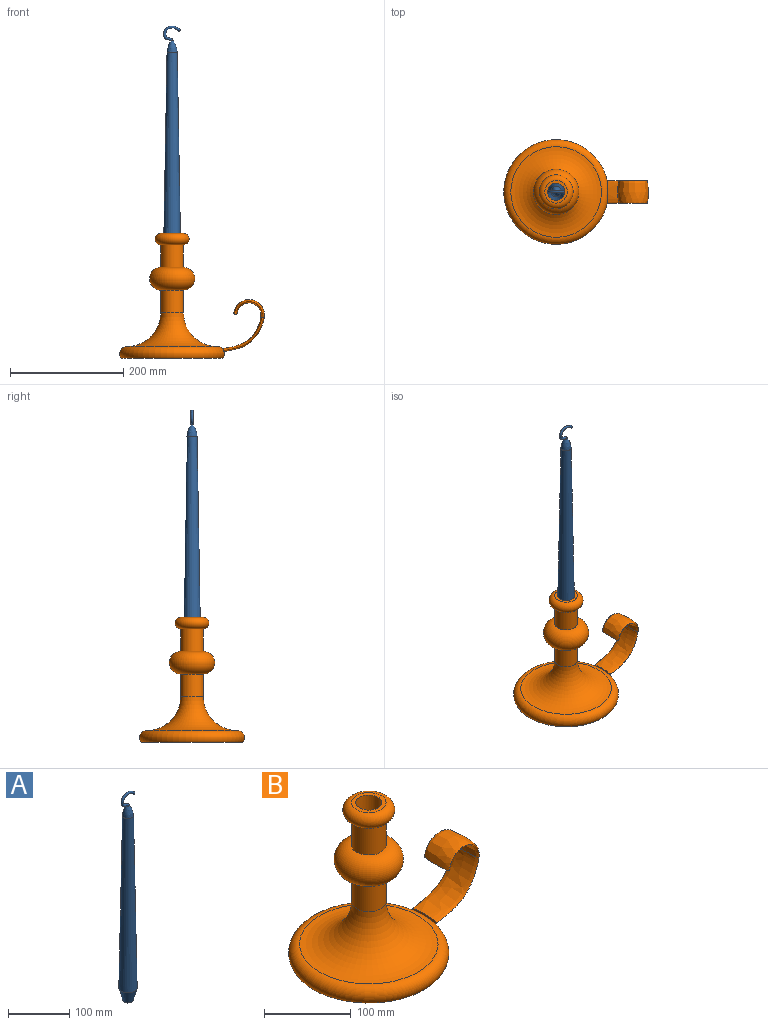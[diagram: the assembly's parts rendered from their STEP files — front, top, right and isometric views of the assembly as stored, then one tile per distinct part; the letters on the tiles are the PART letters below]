
ASSEMBLY  parts=2 mates=1
PART A: 6 faces, bbox 30.4x30x416.7 mm
  f0: plane 4x2.83mm, normal (0.71,0,-0.71), area 12.6mm2, adj f1
  f1: bspline ~30.39x26.67mm, area 700.4mm2, adj f0
  f2: plane 16.6x16.6mm, normal (0,0,-1), area 216.5mm2, adj f3
  f3: cone r=15mm half-angle=15deg, axis (0,0,1), area 1894.6mm2, adj f2,f4
  f4: cone r=15mm half-angle=1deg, axis (0,0,-1), area 25971.3mm2, adj f3,f5
  f5: revolved ~20.38x17.97mm, area 1805.3mm2, adj f4
PART B: 14 faces, bbox 275.8x206.5x227.6 mm
  f0: torus R=80mm, axis (0,0,-1), area 15435mm2, adj f5,f6,f10,f12
  f1: torus R=20mm, axis (0,0,-1), area 12922.2mm2, adj f2,f7
  f2: cylinder r=20mm len=40mm, axis (0,0,-1), area 5026.5mm2, adj f1,f3
  f3: torus R=20mm, axis (0,0,-1), area 5204.5mm2, adj f2,f4
  f4: plane 40x40mm, normal (0,0,1), area 549.8mm2, adj f3,f8
  f5: plane 180x180mm, normal (0,0,-1), area 25446.9mm2, adj f0
  f6: torus R=80mm, axis (0,0,-1), area 24754.6mm2, adj f0,f7
  f7: cylinder r=20mm len=40mm, axis (0,0,-1), area 5026.5mm2, adj f1,f6
  f8: cylinder r=15mm len=50mm, axis (0,0,1), area 4712.4mm2, adj f4,f9
  f9: plane 30x30mm, normal (0,0,1), area 706.9mm2, adj f8
  f10: plane 46.26x11.55mm, normal (-1,0,0), area 140.4mm2, adj f0,f12
  f11: plane 43.99x9.82mm, normal (-0.23,0,-0.97), area 188.5mm2, adj f13
  f12: bspline ~74.57x65.89mm, area 8069.8mm2, adj f0,f10,f13
  f13: bspline ~63.68x40mm, area 6569mm2, adj f11,f12
PLACE A t=(-100.41,-4.1,140.8)mm
PLACE B t=(-100.41,-4.1,-29.2)mm
MATE planar A.f3 <-> B.f8  axis (0,0,-1) through (-100.41,-4.1,140.8)mm
